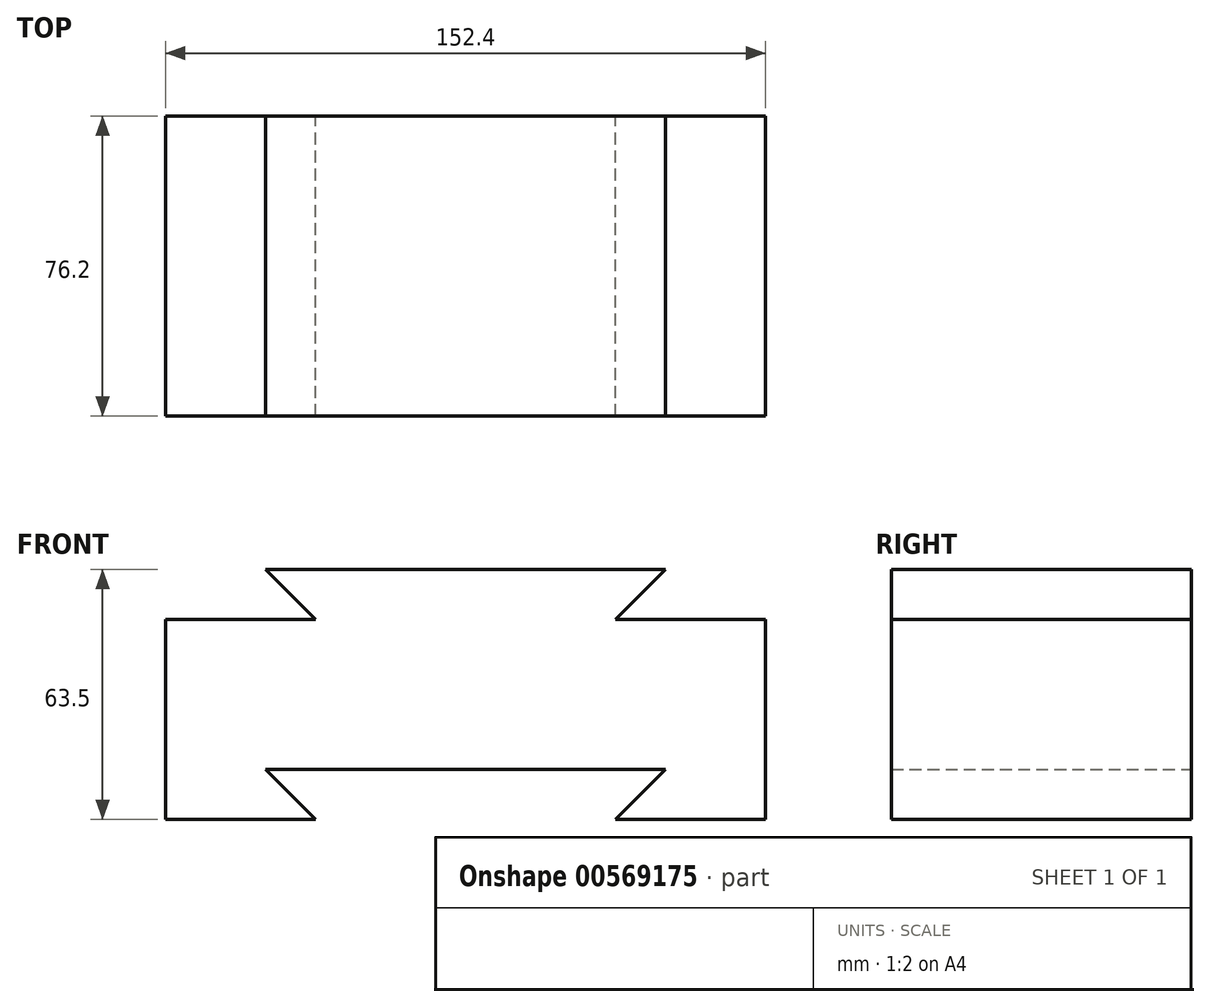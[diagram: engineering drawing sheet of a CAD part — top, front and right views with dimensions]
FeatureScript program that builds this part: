
annotation { "Feature Type Name" : "Feature", "Feature Type Description" : "" }
export const myFeature = defineFeature(function(context is Context, id is Id, definition is map)
    precondition{}
    {
        {
            var Q0;
            Q0=qCreatedBy(makeId("Front.planeOp"),FACE);
            var sketch = newSketch(context, id + "F0", { "sketchPlane" : qUnion([Q0])});
            skLineSegment(sketch, "E0.bottom", {"start": v(-163.35, -2.3) * mm, "end": v(-125.25, -2.3) * mm});
            skLineSegment(sketch, "E0.top", {"start": v(-137.95, -40.4) * mm, "end": v(-36.35, -40.4) * mm});
            skLineSegment(sketch, "E0.left", {"start": v(-163.35, -2.3) * mm, "end": v(-163.35, -40.4) * mm});
            skLineSegment(sketch, "E0.right", {"start": v(-10.95, -2.3) * mm, "end": v(-10.95, -40.4) * mm});
            skLineSegment(sketch, "E1", {"start": v(-49.05, -2.3) * mm, "end": v(-10.95, -2.3) * mm});
            skLineSegment(sketch, "E2", {"start": v(-137.95, 10.4) * mm, "end": v(-125.25, 10.4) * mm});
            skLineSegment(sketch, "E3", {"start": v(-49.05, 10.4) * mm, "end": v(-36.35, 10.4) * mm});
            skLineSegment(sketch, "E4", {"start": v(-137.95, 10.4) * mm, "end": v(-125.25, -2.3) * mm});
            skLineSegment(sketch, "E5", {"start": v(-36.35, 10.4) * mm, "end": v(-49.05, -2.3) * mm});
            skLineSegment(sketch, "E6", {"start": v(-125.25, 10.4) * mm, "end": v(-49.05, 10.4) * mm});
            skLineSegment(sketch, "E7", {"start": v(-163.35, -40.4) * mm, "end": v(-163.35, -53.1) * mm});
            skLineSegment(sketch, "E8", {"start": v(-10.95, -40.4) * mm, "end": v(-10.95, -53.1) * mm});
            skLineSegment(sketch, "E9", {"start": v(-163.35, -53.1) * mm, "end": v(-125.25, -53.1) * mm});
            skLineSegment(sketch, "E10", {"start": v(-49.05, -53.1) * mm, "end": v(-10.95, -53.1) * mm});
            skLineSegment(sketch, "E11", {"start": v(-137.95, -40.4) * mm, "end": v(-125.25, -53.1) * mm});
            skLineSegment(sketch, "E12", {"start": v(-36.35, -40.4) * mm, "end": v(-49.05, -53.1) * mm});
            skSolve(sketch);
        }
        {
            var Q0;
            Q0=makeQuery(id+"F0.imprint","IMPRINT",FACE,{"disambiguationData":[TD([[makeQuery(id+"F0.imprint","IMPRINT",EDGE,{"derivedFrom":sQuery(id+"F0.wireOp",EDGE,"E0.top")}),1.0]])]});
            extrude(context, id + "F1", {"entities" : qUnion([Q0]), "depth" : 76.2 * mm, "offsetDistance" : 25.4 * mm});
        }
    });
